# Revit family: P4TT, 1815, 1818
name_source: partatom
category: Windows
revit_build: Autodesk Revit LT 2016 (Build: 20150220_1215(x64)
units: mm (PartAtom-declared; Revit-internal decimal feet)

## family parameters
Always vertical = Yes
Cut with Voids When Loaded = No
Host = Wall
OmniClass Number = 23.30.20.00
OmniClass Title = Windows
Room Calculation Point = No
Shared = No

## types (2) — shared parameters
Aluminium anodized = Aluminium
Centre vert mullion = 610 mm  [stored 2.00131 ft]
Default Sill Height = 914 mm
Glazing = Glass
Height = 1510 mm  [stored 4.95407 ft]
Manufacturer = Robmeg
Plaster = 5 mm  [stored 0.0164042 ft]
Rough Height = 1219 mm
Side hung = Yes
Top hung = No
URL = http://www.robmeg.co.za
Wall Closure = By host
Width = 1810 mm  [stored 5.93832 ft]

## per-type parameters (varying)
| type | Bottom fixed glass width | Bottom mullion height | Centre fixed glass width | Description | Model | Top mullion |
| P4TT Type- 1815 | 4 mm  [stored 0.0131234 ft] | 300 mm | 4 mm  [stored 0.0131234 ft] | Anodized Aluminium | P4TT 1815 | 605 mm  [stored 1.98491 ft] |
| P4TT Type- 1818 | 6 mm  [stored 0.019685 ft] | 500 mm  [stored 1.64042 ft] | 6 mm  [stored 0.019685 ft] | Anodized Aluminim | P4TT 1818 | 500 mm  [stored 1.64042 ft] |

note: [stored X ft] marks values corroborated as IEEE doubles in the binary element streams (Revit-internal decimal feet)

## geometry (parser evidence)
native form markers: Sweep x3
no freeform markers — native parametric forms only
